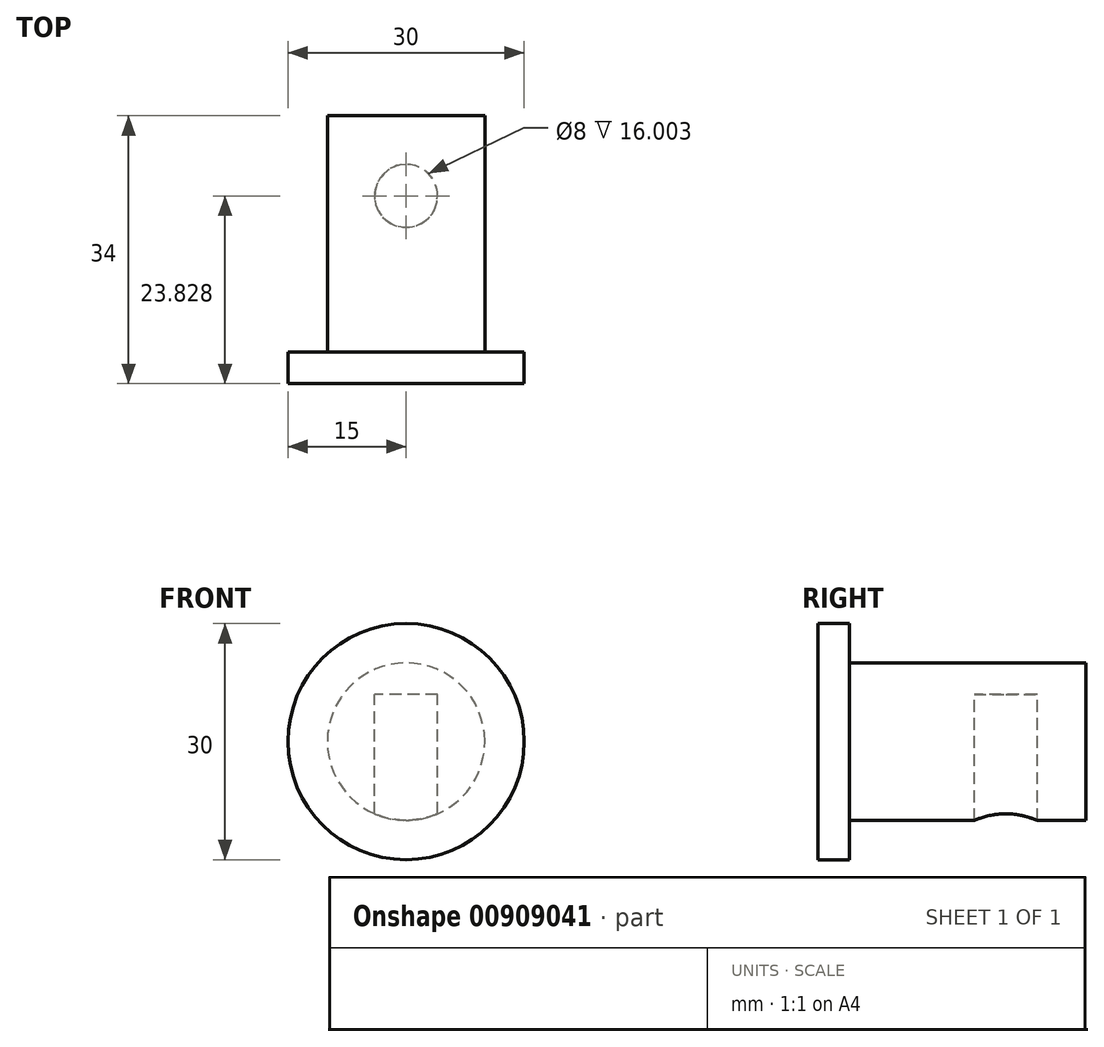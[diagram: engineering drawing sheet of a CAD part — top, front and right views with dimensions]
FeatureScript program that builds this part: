
annotation { "Feature Type Name" : "Feature", "Feature Type Description" : "" }
export const myFeature = defineFeature(function(context is Context, id is Id, definition is map)
    precondition{}
    {
        {
            var Q0;
            Q0=qCreatedBy(makeId("Front.planeOp"),FACE);
            var sketch = newSketch(context, id + "F0", { "sketchPlane" : qUnion([Q0])});
            skCircle(sketch, "E0", {"center": v(0, 0) * mm, "radius": 15 * mm});
            skSolve(sketch);
        }
        {
            var Q0;
            Q0=makeQuery(id+"F0.imprint","IMPRINT",FACE,{"disambiguationData":[TD([[makeQuery(id+"F0.imprint","IMPRINT",EDGE,{"derivedFrom":sQuery(id+"F0.wireOp",EDGE,"E0")}),1.0]])]});
            extrude(context, id + "F1", {"entities" : qUnion([Q0]), "depth" : 4 * mm, "offsetDistance" : 25 * mm});
        }
        {
            var Q0;
            Q0=makeQuery(id+"F1.opExtrude","CAP_FACE",FACE,{"disambiguationData":[OSD([sQuery(id+"F0.wireOp",EDGE,"E0")])],"isStart":true});
            var sketch = newSketch(context, id + "F2", { "sketchPlane" : qUnion([Q0])});
            skCircle(sketch, "E1", {"center": v(0, 0) * mm, "radius": 10 * mm});
            skSolve(sketch);
        }
        {
            var Q0;
            Q0=makeQuery(id+"F2.imprint","IMPRINT",FACE,{"disambiguationData":[TD([[makeQuery(id+"F2.imprint","IMPRINT",EDGE,{"derivedFrom":sQuery(id+"F2.wireOp",EDGE,"E1")}),1.0]])]});
            var Q1;
            Q1=sQuery(id+"F2.wireOp",EDGE,"E1");
            extrude(context, id + "F3", {"entities" : qUnion([Q0]), "operationType" : NewBodyOperationType.ADD, "surfaceEntities" : qUnion([Q1]), "depth" : 30 * mm, "offsetDistance" : 25 * mm});
        }
        {
            var Q0;
            Q0=qCreatedBy(makeId("Top.planeOp"),FACE);
            var sketch = newSketch(context, id + "F4", { "sketchPlane" : qUnion([Q0])});
            skCircle(sketch, "E2", {"center": v(0, 19.83) * mm, "radius": 4 * mm});
            skSolve(sketch);
        }
        {
            var Q0;
            Q0 = qSketchRegion(id + "F4", true);
            var Q1;
            Q1=sQuery(id+"F4.wireOp",EDGE,"E2");
            extrude(context, id + "F5", {"entities" : qUnion([Q0]), "operationType" : NewBodyOperationType.REMOVE, "surfaceEntities" : qUnion([Q1]), "oppositeDirection" : true, "depth" : 27 * mm, "offsetDistance" : 25 * mm});
        }
        {
            var Q0;
            Q0 = qSketchRegion(id + "F4", true);
            extrude(context, id + "F6", {"entities" : qUnion([Q0]), "operationType" : NewBodyOperationType.REMOVE, "depth" : 6 * mm, "offsetDistance" : 25 * mm});
        }
    });
